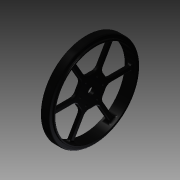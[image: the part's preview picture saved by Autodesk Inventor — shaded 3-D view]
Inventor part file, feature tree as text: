
AUTODESK INVENTOR PART (.ipt)
format: ipt  version: 2015 (Build 190159000, 159)  size: 607,744 bytes
history: native  units: mm
features: fillet x6, extrude x4, sketch x2, other x1
ambient origin geometry x8: Origin, YZ Plane, XZ Plane, XY Plane, X Axis, Y Axis, Z Axis, Center Point
bodies: Body1 (feature_tree)
feature tree (13):
  other  "Sólido1"
  sketch  "Boceto1"  dims[d0=76.5mm d1=3.0mm]
  extrude  "Extrusión1"  Depth=3.0mm
  extrude  "Extrusión2"  Depth=0.2mm TaperAngle=0.0deg
  fillet  "Empalme1"  Radius=1.0mm
  extrude  "Extrusión3"  Depth=0.2mm TaperAngle=0.0deg
  extrude  "Extrusión4"  Depth=0.2mm TaperAngle=360.0deg
  fillet  "Empalme2"  Radius=3.0mm
  fillet  "Empalme3"  Radius=5.0mm
  fillet  "Empalme4"  Radius=2.0mm
  fillet  "Empalme5"  Radius=5.0mm
  fillet  "Empalme6"  Radius=1.0mm
  sketch  "Boceto2"  dims[d2=10.0mm d3=0.0mm d4=7.0mm d5=0.0mm d6=1.0mm d7=3.0mm d8=0.0mm d9=60.0mm d11=360.0deg d13=3.0mm d14=0.0mm d15=5.0mm d16=2.0mm d17=5.0mm d18=1.0mm d19=0.2mm]
